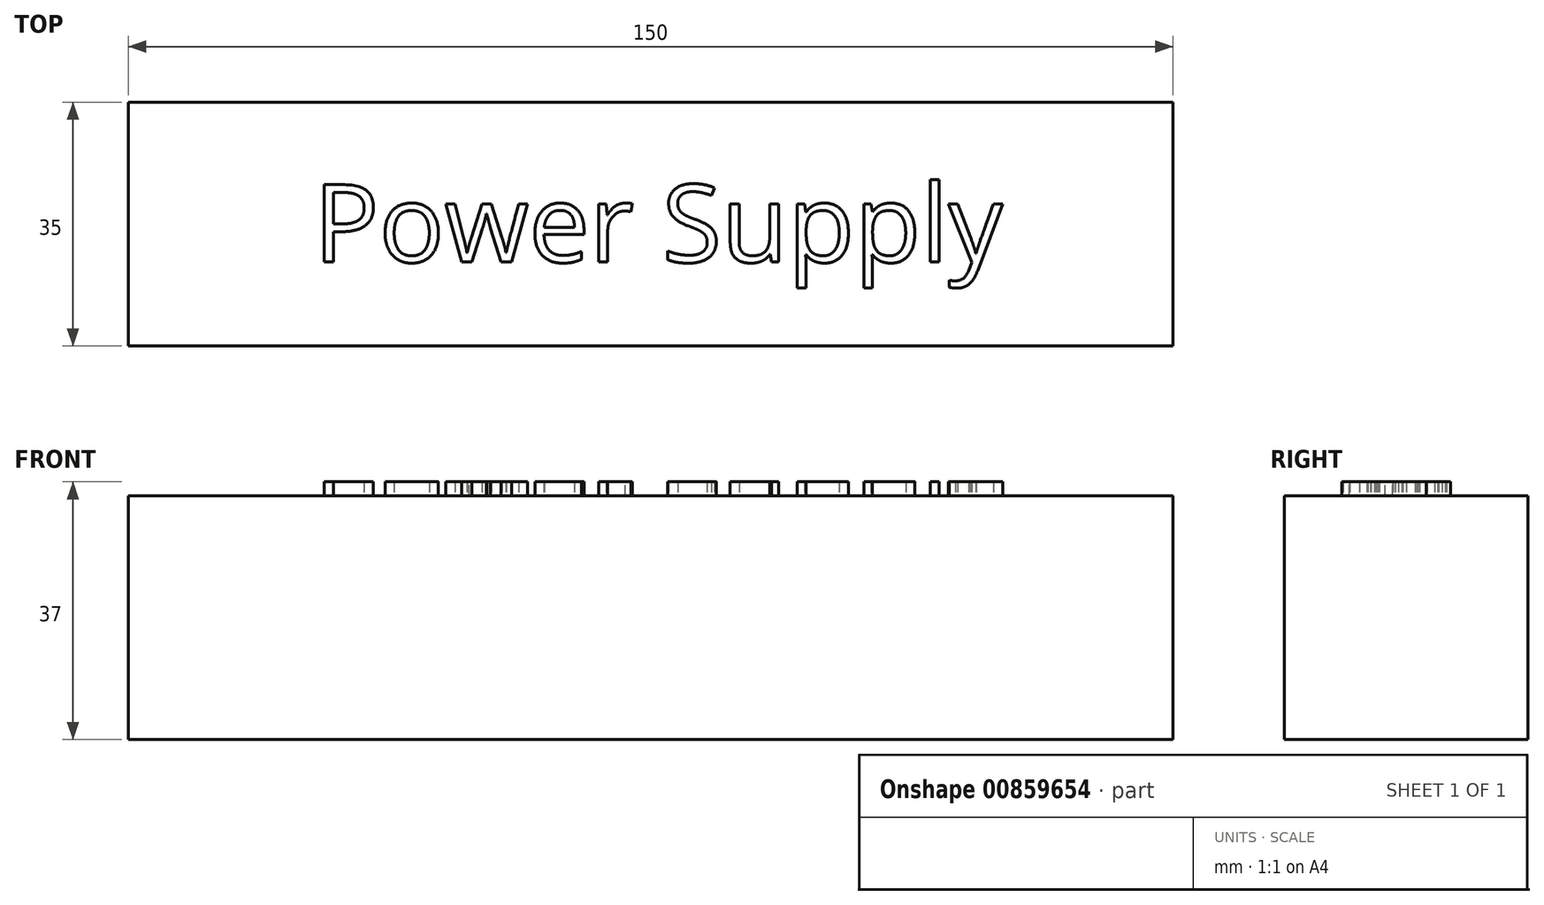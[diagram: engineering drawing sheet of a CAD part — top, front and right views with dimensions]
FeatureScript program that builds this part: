
annotation { "Feature Type Name" : "Feature", "Feature Type Description" : "" }
export const myFeature = defineFeature(function(context is Context, id is Id, definition is map)
    precondition{}
    {
        {
            var Q0;
            Q0=qCreatedBy(makeId("Top.planeOp"),FACE);
            var sketch = newSketch(context, id + "F0", { "sketchPlane" : qUnion([Q0])});
            skLineSegment(sketch, "E0.bottom", {"start": v(75, -17.5) * mm, "end": v(-75, -17.5) * mm});
            skLineSegment(sketch, "E0.top", {"start": v(75, 17.5) * mm, "end": v(-75, 17.5) * mm});
            skLineSegment(sketch, "E0.left", {"start": v(75, -17.5) * mm, "end": v(75, 17.5) * mm});
            skLineSegment(sketch, "E0.right", {"start": v(-75, -17.5) * mm, "end": v(-75, 17.5) * mm});
            skPoint(sketch, "E0.middle", {"position": v(0, 0) * mm});
            skSolve(sketch);
        }
        {
            var Q0;
            Q0=makeQuery(id+"F0.imprint","IMPRINT",FACE,{"disambiguationData":[TD([[makeQuery(id+"F0.imprint","IMPRINT",EDGE,{"derivedFrom":sQuery(id+"F0.wireOp",EDGE,"E0.bottom")}),-1.0]])]});
            extrude(context, id + "F1", {"entities" : qUnion([Q0]), "depth" : 35 * mm, "offsetDistance" : 25 * mm});
        }
        {
            var Q0;
            Q0=makeQuery(id+"F1.opExtrude","CAP_FACE",FACE,{"disambiguationData":[OSD([sQuery(id+"F0.wireOp",EDGE,"E0.bottom"),sQuery(id+"F0.wireOp",EDGE,"E0.top"),sQuery(id+"F0.wireOp",EDGE,"E0.left"),sQuery(id+"F0.wireOp",EDGE,"E0.right")])],"isStart":false});
            cPlane(context, id + "F2", {"entities" : qUnion([Q0]), "cplaneType" : CPlaneType.OFFSET, "offset" : 0 * mm, "width" : 150 * mm, "height" : 150 * mm});
        }
        {
            var Q0;
            Q0=qCreatedBy(id+"F2.planeOp",FACE);
            var sketch = newSketch(context, id + "F3", { "sketchPlane" : qUnion([Q0])});
            skText(sketch, "E1", { "text": "Power Supply", "fontName": "OpenSans-Regular.ttf"});
            const initialGuessF3  = {"E1": [-0.0484, -0.00545, 1, 0, 0.01121]};
            skSetInitialGuess(sketch, initialGuessF3);
            skSolve(sketch);
        }
        {
            var Q0;
            Q0 = qSketchRegion(id + "F3", true);
            extrude(context, id + "F4", {"entities" : qUnion([Q0]), "operationType" : NewBodyOperationType.ADD, "depth" : 2 * mm, "offsetDistance" : 25 * mm});
        }
    });
